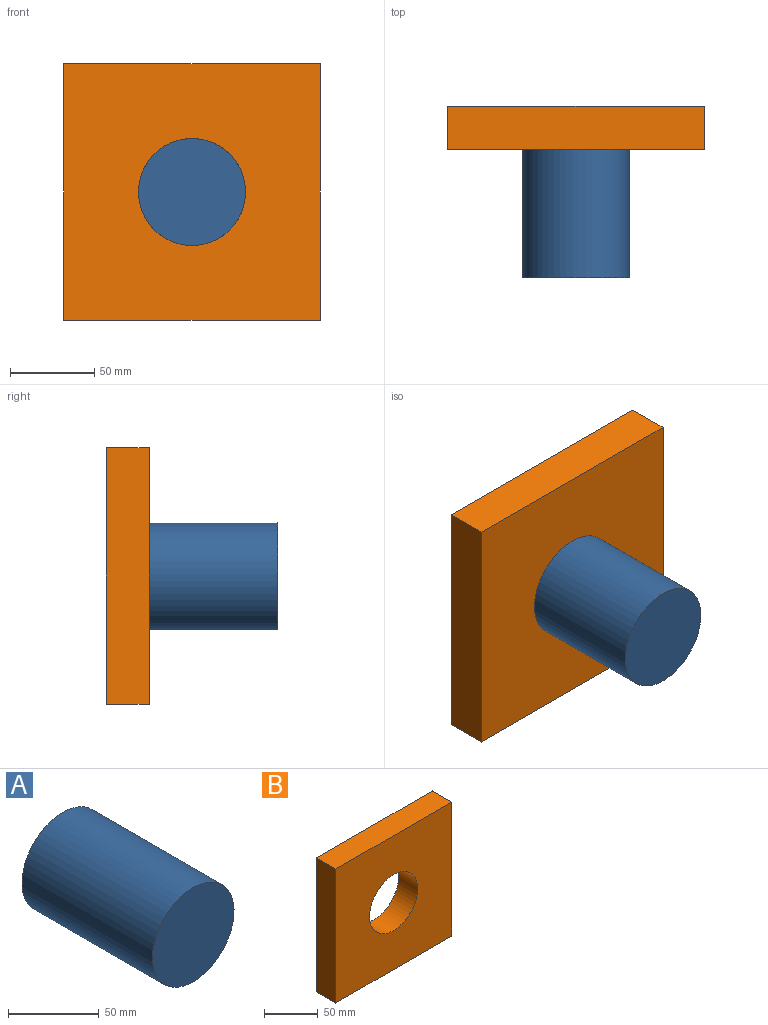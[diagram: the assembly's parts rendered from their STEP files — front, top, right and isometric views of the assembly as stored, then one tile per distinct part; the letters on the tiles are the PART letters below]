
ASSEMBLY  parts=2 mates=1
PART A: 3 faces, bbox 63.5x101.6x63.5 mm
  f0: cylinder r=31.75mm len=101.6mm, axis (0,1,0), area 20268.3mm2, adj f1,f2
  f1: plane 63.5x63.5mm, normal (0,-1,0), area 3166.9mm2, adj f0
  f2: plane 63.5x63.5mm, normal (0,1,0), area 3166.9mm2, adj f0
PART B: 7 faces, bbox 152.4x25.4x152.4 mm
  f0: plane 152.4x25.4mm, normal (0,0,1), area 3871mm2, adj f1,f4,f5,f6
  f1: plane 152.4x25.4mm, normal (-1,0,0), area 3871mm2, adj f0,f2,f5,f6
  f2: plane 152.4x25.4mm, normal (0,0,-1), area 3871mm2, adj f1,f4,f5,f6
  f3: cylinder r=31.75mm len=63.5mm, axis (0,1,0), area 5067.1mm2, adj f5,f6
  f4: plane 152.4x25.4mm, normal (1,0,0), area 3871mm2, adj f0,f2,f5,f6
  f5: plane 152.4x152.4mm, normal (0,-1,0), area 20058.8mm2, adj f0,f1,f2,f3,f4
  f6: plane 152.4x152.4mm, normal (0,1,0), area 20058.8mm2, adj f0,f1,f2,f3,f4
PLACE A t=(155.47,58.42,-22.54)mm fixed
PLACE B rot(axis=(0,1,0),90deg) t=(0,58.42,0)mm
MATE cylindrical A.f0 <-> B.f3  axis (0,-1,0) through (0,-43.18,0)mm
